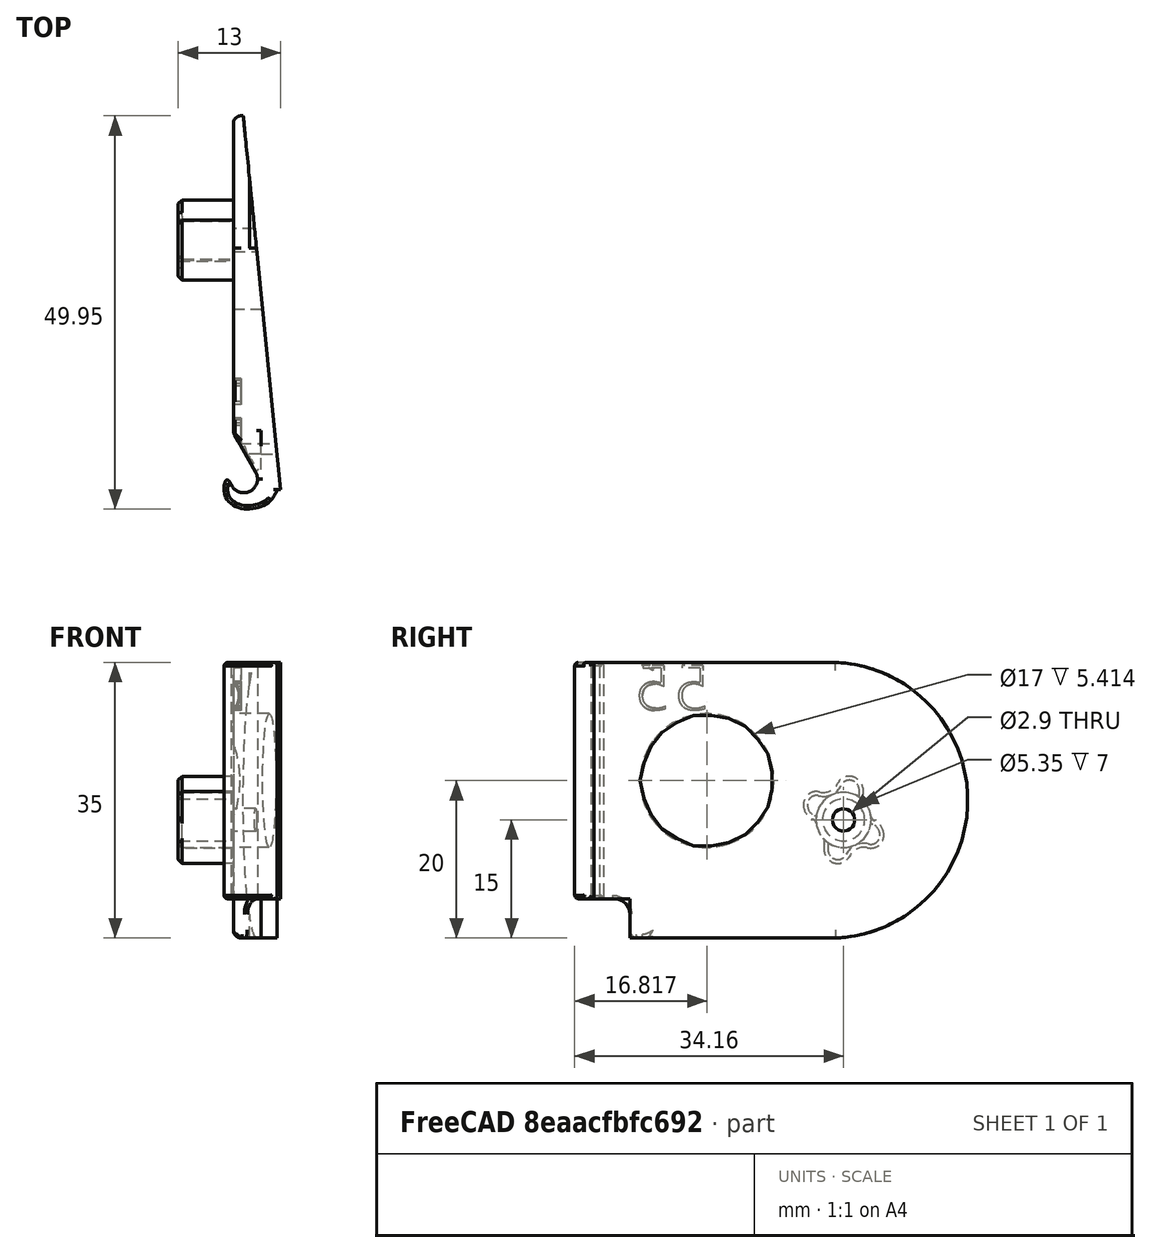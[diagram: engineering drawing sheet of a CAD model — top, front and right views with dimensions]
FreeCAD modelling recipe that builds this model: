
FCSTD DOCUMENT  (FreeCAD 0.18R)
Label: hinge-left-159deg
License: All rights reserved
LicenseURL: http://en.wikipedia.org/wiki/All_rights_reserved
objects: App::FeaturePython×4, Part::FeaturePython×2, Part::Part2DObjectPython×1, Part::Extrusion×1, Part::Cut×1
note: 5 computed .brp shape members not serialized (recipe doc carries the construction recipe); baked Part::Feature solids carry a one-line shape summary decoded from their .brp

FEATURE [Part::FeaturePython] bracket_left_001  label="bracket-left_001"  # a2plus imported part (geometry in sourceFile) (typed FeaturePython)
  a2p_Version = V0.1
  fixedPosition = true
  objectType = a2pPart
  sourceFile = ./parts/bracket-left.fcstd
  subassemblyImport = false
  timeLastImport = 1.60454e+09
  updateColors = true
FEATURE [Part::FeaturePython] pillar_base_001  label="pillar-base_001"  # a2plus imported part (geometry in sourceFile) (typed FeaturePython)
  Placement = pos=(0.000601362,0.00261841,-0.00477498) rot=(1,0,0;0.000175rad)
  a2p_Version = V0.1
  fixedPosition = false
  objectType = a2pPart
  sourceFile = ./parts/pillar-base.fcstd
  subassemblyImport = false
  timeLastImport = 1.60452e+09
  updateColors = true
FEATURE [Part::Part2DObjectPython] ShapeString  # Draft 2D object (typed FeaturePython)
  FontFile = <path>
  Placement = pos=(1.61,10.5,29) rot=(0.57735,-0.57735,-0.57735;2.0944rad)
  Size = 6
  String = 55
  Tracking = 0
FEATURE [Part::Extrusion] Extrude
  Base = -> ShapeString
  Dir = (-1,-1e-16,2e-16)
  DirMode = 2
  FaceMakerClass = Part::FaceMakerBullseye
  LengthFwd = 2
  LengthRev = 0
  Solid = false
  Symmetric = false
FEATURE [App::FeaturePython] axisCoincident_001  label="axisCoincident_001__bracket-left_001"  # a2plus constraint (typed FeaturePython)
  Object1 = pillar_base_001
  Object2 = bracket_left_001
  ParentTreeObject = -> pillar_base_001
  SubElement1 = Face17
  SubElement2 = Face39
  Suppressed = false
  Type = axial
  directionConstraint = 1
  lockRotation = false
FEATURE [App::FeaturePython] axisCoincident_001_mirror  label="axisCoincident_001__pillar-base_001"  # a2plus constraint (typed FeaturePython)
  Object1 = pillar_base_001
  Object2 = bracket_left_001
  ParentTreeObject = -> bracket_left_001
  SubElement1 = Face17
  SubElement2 = Face39
  Suppressed = false
  Type = axial
  directionConstraint = 1
  lockRotation = false
FEATURE [App::FeaturePython] planeCoincident_001  label="planeCoincident_001__bracket-left_001"  # a2plus constraint (typed FeaturePython)
  Object1 = pillar_base_001
  Object2 = bracket_left_001
  ParentTreeObject = -> pillar_base_001
  SubElement1 = Face1
  SubElement2 = Face65
  Suppressed = false
  Type = plane
  directionConstraint = 0
  offset = 0
FEATURE [App::FeaturePython] planeCoincident_001_mirror  label="planeCoincident_001__pillar-base_001"  # a2plus constraint (typed FeaturePython)
  Object1 = pillar_base_001
  Object2 = bracket_left_001
  ParentTreeObject = -> bracket_left_001
  SubElement1 = Face1
  SubElement2 = Face65
  Suppressed = false
  Type = plane
  directionConstraint = 0
  offset = 0
FEATURE [Part::Cut] Cut
  Base = -> bracket_left_001
  Tool = -> Extrude
note: 1 file-system path scrubbed to <path> (originals preserved in the JSON sidecar)
